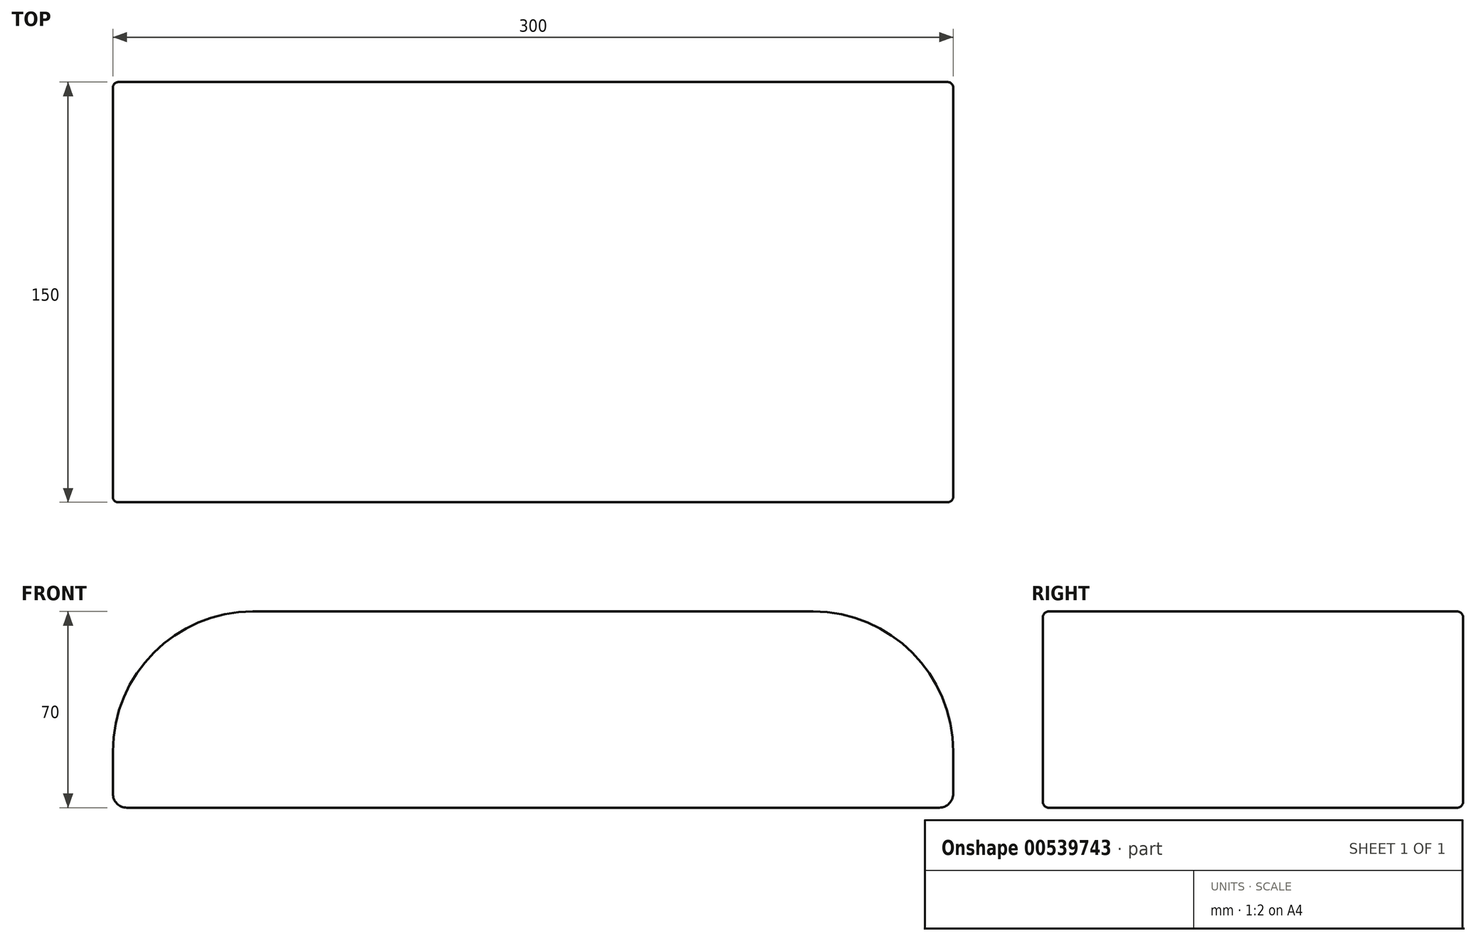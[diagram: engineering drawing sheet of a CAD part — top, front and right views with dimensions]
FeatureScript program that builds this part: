
annotation { "Feature Type Name" : "Feature", "Feature Type Description" : "" }
export const myFeature = defineFeature(function(context is Context, id is Id, definition is map)
    precondition{}
    {
        {
            var Q0;
            Q0=qCreatedBy(makeId("Top.planeOp"),FACE);
            var sketch = newSketch(context, id + "F0", { "sketchPlane" : qUnion([Q0])});
            skLineSegment(sketch, "E0.bottom", {"start": v(0, 3.75) * mm, "end": v(300, 3.75) * mm});
            skLineSegment(sketch, "E0.top", {"start": v(0, 153.75) * mm, "end": v(300, 153.75) * mm});
            skLineSegment(sketch, "E0.left", {"start": v(0, 3.75) * mm, "end": v(0, 153.75) * mm});
            skLineSegment(sketch, "E0.right", {"start": v(300, 3.75) * mm, "end": v(300, 153.75) * mm});
            skSolve(sketch);
        }
        {
            var Q0;
            Q0=makeQuery(id+"F0.imprint","IMPRINT",FACE,{"disambiguationData":[TD([[makeQuery(id+"F0.imprint","IMPRINT",EDGE,{"derivedFrom":sQuery(id+"F0.wireOp",EDGE,"E0.bottom")}),1.0]])]});
            extrude(context, id + "F1", {"entities" : qUnion([Q0]), "depth" : 70 * mm, "offsetDistance" : 25 * mm});
        }
        {
            var Q0;
            Q0=makeQuery(id+"F1.opExtrude","CAP_EDGE",EDGE,{"disambiguationData":[OSD([sQuery(id+"F0.wireOp",EDGE,"E0.left")])],"isStart":false});
            var Q1;
            Q1=makeQuery(id+"F1.opExtrude","CAP_EDGE",EDGE,{"disambiguationData":[OSD([sQuery(id+"F0.wireOp",EDGE,"E0.right")])],"isStart":false});
            fillet(context, id + "F2", {"entities" : qUnion([Q0, Q1]), "radius" : 50 * mm, "tangentPropagation" : true, "allowEdgeOverflow" : false});
        }
        {
            var Q0;
            Q0=makeQuery(id+"F1.opExtrude","CAP_EDGE",EDGE,{"disambiguationData":[OSD([sQuery(id+"F0.wireOp",EDGE,"E0.left")])],"isStart":true});
            var Q1;
            Q1=makeQuery(id+"F1.opExtrude","CAP_EDGE",EDGE,{"disambiguationData":[OSD([sQuery(id+"F0.wireOp",EDGE,"E0.right")])],"isStart":true});
            fillet(context, id + "F3", {"entities" : qUnion([Q0, Q1]), "radius" : 5 * mm, "tangentPropagation" : true, "allowEdgeOverflow" : false});
        }
        {
            var Q0;
            Q0=makeQuery(id+"F1.opExtrude","CAP_EDGE",EDGE,{"disambiguationData":[OSD([sQuery(id+"F0.wireOp",EDGE,"E0.bottom")])],"isStart":false});
            var Q1;
            Q1=makeQuery(id+"F1.opExtrude","CAP_EDGE",EDGE,{"disambiguationData":[OSD([sQuery(id+"F0.wireOp",EDGE,"E0.top")])],"isStart":false});
            var Q2;
            {var subQ0=sQuery(id+"F0.wireOp",EDGE,"E0.right");Q2=makeQuery(id+"F2.opFillet","BLEND_EDGE",EDGE,{"blendedFrom":[makeQuery(id+"F1.opExtrude","CAP_EDGE",EDGE,{"disambiguationData":[OSD([subQ0])],"isStart":false}),makeQuery(id+"F1.opExtrude","CAP_FACE",FACE,{"disambiguationData":[OSD([sQuery(id+"F0.wireOp",EDGE,"E0.bottom"),sQuery(id+"F0.wireOp",EDGE,"E0.top"),sQuery(id+"F0.wireOp",EDGE,"E0.left"),subQ0])],"isStart":true})],"blendedInto":[makeQuery(id+"F1.opExtrude","CAP_FACE",FACE,{"disambiguationData":[OSD([sQuery(id+"F0.wireOp",EDGE,"E0.bottom"),sQuery(id+"F0.wireOp",EDGE,"E0.top"),sQuery(id+"F0.wireOp",EDGE,"E0.left"),subQ0])],"isStart":true})]});}
            var Q3;
            Q3=makeQuery(id+"F1.opExtrude","CAP_EDGE",EDGE,{"disambiguationData":[OSD([sQuery(id+"F0.wireOp",EDGE,"E0.bottom")])],"isStart":true});
            var Q4;
            Q4=makeQuery(id+"F1.opExtrude","CAP_EDGE",EDGE,{"disambiguationData":[OSD([sQuery(id+"F0.wireOp",EDGE,"E0.top")])],"isStart":true});
            var Q5;
            {var subQ0=sQuery(id+"F0.wireOp",EDGE,"E0.left");Q5=makeQuery(id+"F2.opFillet","BLEND_EDGE",EDGE,{"blendedFrom":[makeQuery(id+"F1.opExtrude","CAP_EDGE",EDGE,{"disambiguationData":[OSD([subQ0])],"isStart":false}),makeQuery(id+"F1.opExtrude","CAP_FACE",FACE,{"disambiguationData":[OSD([sQuery(id+"F0.wireOp",EDGE,"E0.bottom"),sQuery(id+"F0.wireOp",EDGE,"E0.top"),subQ0,sQuery(id+"F0.wireOp",EDGE,"E0.right")])],"isStart":true})],"blendedInto":[makeQuery(id+"F1.opExtrude","CAP_FACE",FACE,{"disambiguationData":[OSD([sQuery(id+"F0.wireOp",EDGE,"E0.bottom"),sQuery(id+"F0.wireOp",EDGE,"E0.top"),subQ0,sQuery(id+"F0.wireOp",EDGE,"E0.right")])],"isStart":true})]});}
            fillet(context, id + "F4", {"entities" : qUnion([Q0, Q1, Q2, Q3, Q4, Q5]), "radius" : 2 * mm, "tangentPropagation" : true, "allowEdgeOverflow" : false});
        }
    });
